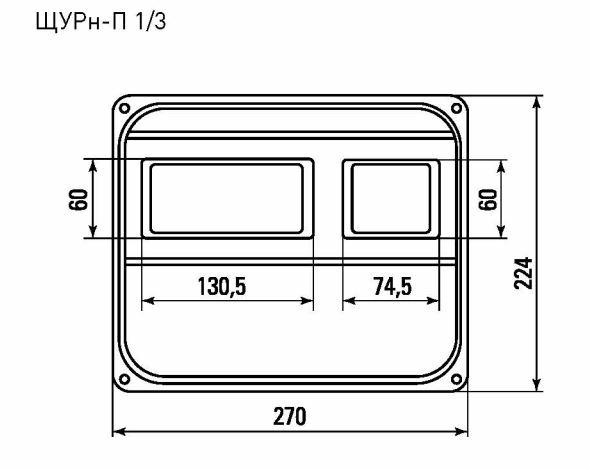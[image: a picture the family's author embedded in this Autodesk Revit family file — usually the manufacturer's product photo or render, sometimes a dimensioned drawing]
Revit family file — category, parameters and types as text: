
# Revit family: EKF_EE_Короб_КСС(1890х300х150)_Basic
name_source: partatom
category: Электрооборудование
units: mm (PartAtom-declared; Revit-internal decimal feet)

## family parameters
Всегда вертикально = Да
На основе рабочей плоскости = Нет
Общий = Нет
При загрузке вырезать с полостями = Нет
Размер круглого соединителя = Использовать диаметр
Тип детали = Силовой щит
Точка расчета площади = Да

## types (1)
- Короб КСС (1890х300х150) EKF Basic
    ADSK_Единица измерения = компл.
    ADSK_Завод-изготовитель = EKF
    ADSK_Классификация нагрузок = Прочее
    ADSK_Код изделия = uerm-kss-1890
    ADSK_Количество = 1
    ADSK_Количество фаз = 3
    ADSK_Коэффициент мощности = 1
    ADSK_Марка = Короб КСС
    ADSK_Масса = 0
    ADSK_Материал = RAL 7035_Сталь
    ADSK_Наименование = Короб КСС (1890х300х150) EKF BasicКороб КСС (1890х300х150) EKF Basic
    ADSK_Напряжение = 400 В
    ADSK_Номинальная мощность = 0 Вт
    ADSK_Обозначение = Короб КСС
    ADSK_Полная мощность = 0 В·А
    ADSK_Размер_Высота = 1890 мм
    ADSK_Размер_Глубина = 150 мм
    ADSK_Размер_Ширина = 300 мм
    ADSK_Ток = 125 А
    Изготовитель = EKF
    Количество DIN-реек = 0
    Количество модулей на DIN-рейке = 0
    Максимальное количество модулей = 0
    Описание = Короб КСС (1890х300х150) EKF BasicКороб КСС (1890х300х150) EKF Basic
    Серия номенклатуры = Basic
    Степень защиты IP = IP31
    ТВ = EKF
    Тип = 202 мм
    Тип установки = Навесной
